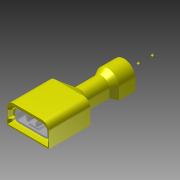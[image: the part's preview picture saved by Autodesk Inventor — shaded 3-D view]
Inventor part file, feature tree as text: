
AUTODESK INVENTOR PART (.ipt)
format: ipt  version: 2011 (Build 150239000, 239)  size: 271,872 bytes
history: native  units: in
note: dims shown in document units (in); Inventor stores cm internally (conversion verified against a paired STEP export)
features: other x4, plane x2, imported_body x1, sketch x1
ambient origin geometry x8: Origin, YZ Plane, XZ Plane, XY Plane, X Axis, Y Axis, Z Axis, Center Point
bodies: Solid1 (feature_tree)
feature tree (8):
  imported_body  "Base1"
  sketch  "Sketch1"  dims[d0=0.125in d1=0.25in]
  other  "Work Point2"
  other  "Work Point3"
  plane  "Work Plane1"
  other  "Work Axis1"
  plane  "Work Plane2"
  other  "Work Axis2"
